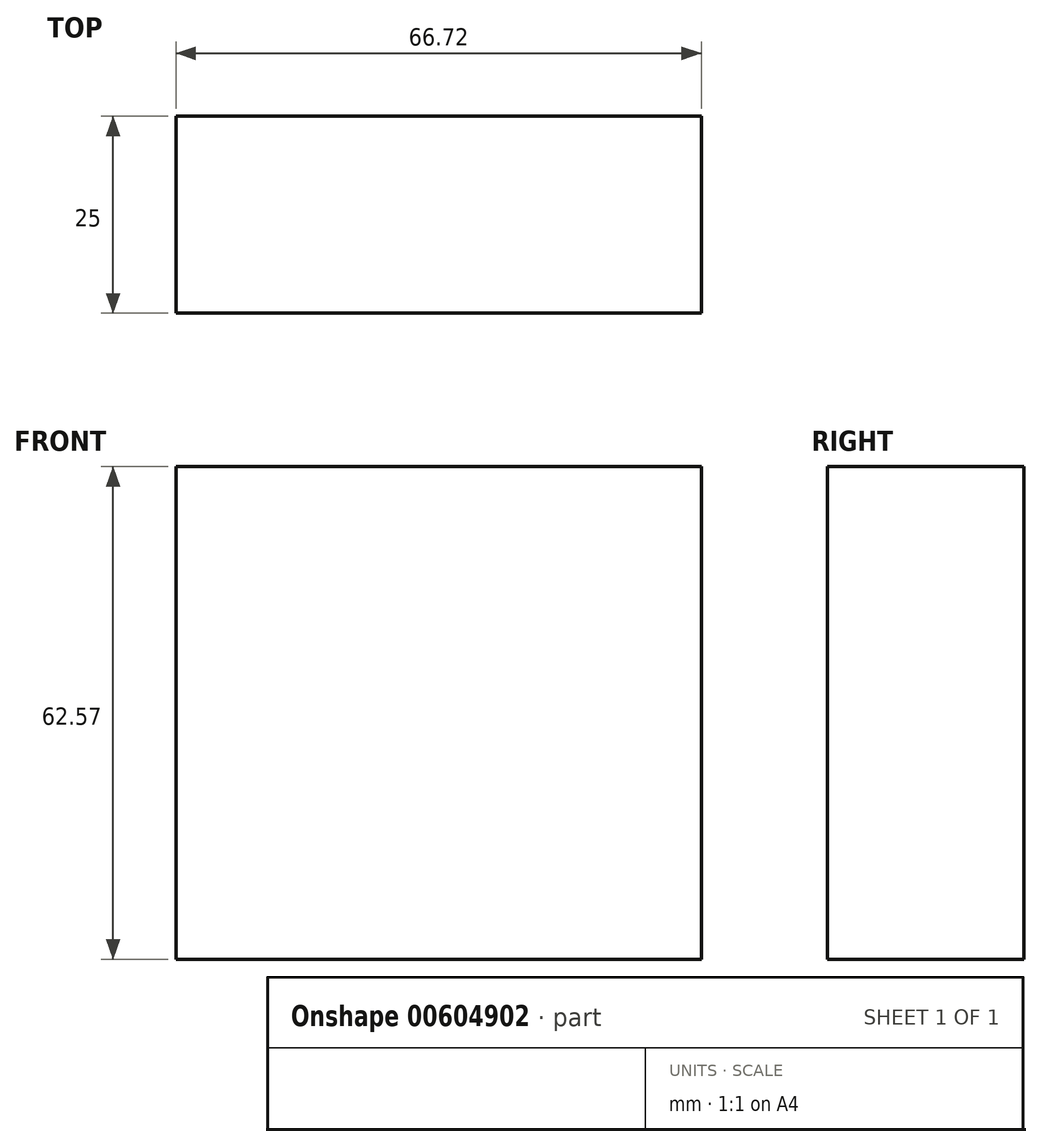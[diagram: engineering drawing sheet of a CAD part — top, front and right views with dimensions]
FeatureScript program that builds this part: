
annotation { "Feature Type Name" : "Feature", "Feature Type Description" : "" }
export const myFeature = defineFeature(function(context is Context, id is Id, definition is map)
    precondition{}
    {
        {
            var Q0;
            Q0=qCreatedBy(makeId("Front.planeOp"),FACE);
            var sketch = newSketch(context, id + "F0", { "sketchPlane" : qUnion([Q0])});
            skLineSegment(sketch, "E0.bottom", {"start": v(-90.53, 91.77) * mm, "end": v(-23.8, 91.77) * mm});
            skLineSegment(sketch, "E0.top", {"start": v(-90.53, 29.2) * mm, "end": v(-23.8, 29.2) * mm});
            skLineSegment(sketch, "E0.left", {"start": v(-90.53, 91.77) * mm, "end": v(-90.53, 29.2) * mm});
            skLineSegment(sketch, "E0.right", {"start": v(-23.8, 91.77) * mm, "end": v(-23.8, 29.2) * mm});
            skSolve(sketch);
        }
        {
            var Q0;
            Q0 = qSketchRegion(id + "F0", true);
            extrude(context, id + "F1", {"entities" : qUnion([Q0]), "depth" : 25 * mm, "offsetDistance" : 25 * mm});
        }
    });
